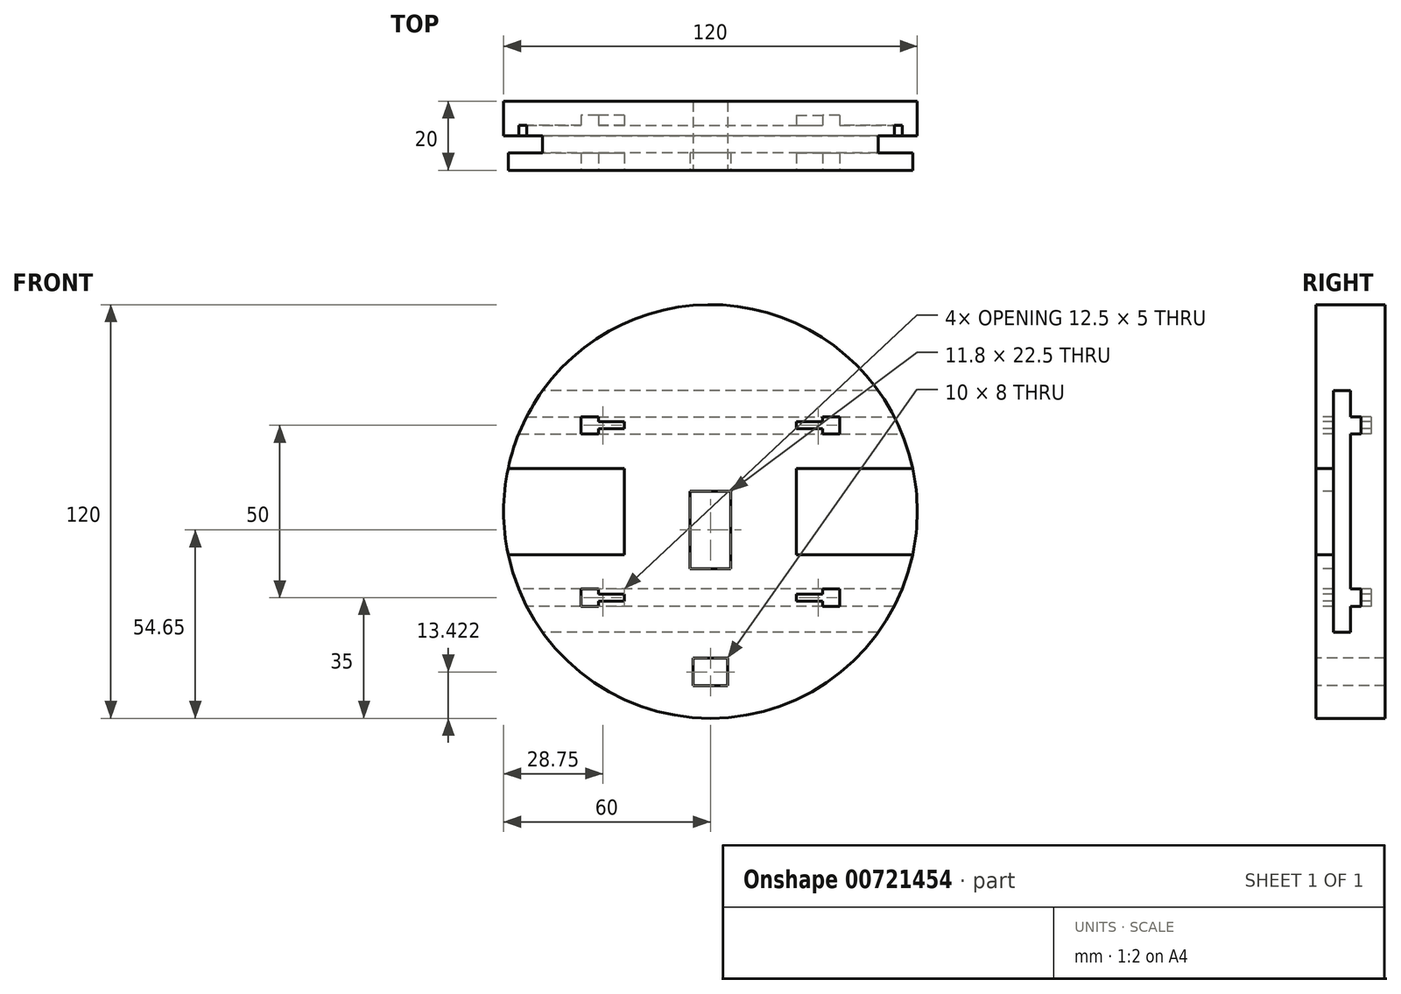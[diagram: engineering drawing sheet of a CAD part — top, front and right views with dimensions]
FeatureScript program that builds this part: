
annotation { "Feature Type Name" : "Feature", "Feature Type Description" : "" }
export const myFeature = defineFeature(function(context is Context, id is Id, definition is map)
    precondition{}
    {
        {
            var Q0;
            Q0=qCreatedBy(makeId("Front.planeOp"),FACE);
            var sketch = newSketch(context, id + "F0", { "sketchPlane" : qUnion([Q0])});
            skCircle(sketch, "E0", {"center": v(0, 0) * mm, "radius": 60 * mm});
            skSolve(sketch);
        }
        {
            var Q0;
            Q0=makeQuery(id+"F0.imprint","IMPRINT",FACE,{"disambiguationData":[TD([[makeQuery(id+"F0.imprint","IMPRINT",EDGE,{"derivedFrom":sQuery(id+"F0.wireOp",EDGE,"E0")}),1.0]])]});
            extrude(context, id + "F1", {"entities" : qUnion([Q0]), "depth" : 20 * mm, "offsetDistance" : 25.4 * mm});
        }
        {
            var Q0;
            Q0=makeQuery(id+"F1.opExtrude","CAP_FACE",FACE,{"disambiguationData":[OSD([sQuery(id+"F0.wireOp",EDGE,"E0")])],"isStart":false});
            var sketch = newSketch(context, id + "F2", { "sketchPlane" : qUnion([Q0])});
            skLineSegment(sketch, "E1.bottom", {"start": v(-60, 12.5) * mm, "end": v(60, 12.5) * mm});
            skLineSegment(sketch, "E1.top", {"start": v(-60, -12.5) * mm, "end": v(60, -12.5) * mm});
            skLineSegment(sketch, "E1.left", {"start": v(-60, 12.5) * mm, "end": v(-60, -12.5) * mm});
            skLineSegment(sketch, "E1.right", {"start": v(60, 12.5) * mm, "end": v(60, -12.5) * mm});
            skPoint(sketch, "E1.middle", {"position": v(0, 0) * mm});
            skLineSegment(sketch, "E2", {"start": v(-25, 12.5) * mm, "end": v(-25, -12.5) * mm});
            skLineSegment(sketch, "E3", {"start": v(25, 12.5) * mm, "end": v(25, -12.5) * mm});
            skSolve(sketch);
        }
        {
            var Q0;
            {var subQ4=sQuery(id+"F2.wireOp",EDGE,"E2");Q0=makeQuery(id+"F2.imprint","IMPRINT",FACE,{"disambiguationData":[TD([[makeQuery(id+"F2.imprint","IMPRINT",EDGE,{"derivedFrom":subQ4}),-1.0]])]});}
            var Q1;
            {var subQ4=sQuery(id+"F2.wireOp",EDGE,"E3");Q1=makeQuery(id+"F2.imprint","IMPRINT",FACE,{"disambiguationData":[TD([[makeQuery(id+"F2.imprint","IMPRINT",EDGE,{"derivedFrom":subQ4}),1.0]])]});}
            extrude(context, id + "F3", {"entities" : qUnion([Q0, Q1]), "operationType" : NewBodyOperationType.REMOVE, "oppositeDirection" : true, "depth" : 10 * mm, "offsetDistance" : 25.4 * mm});
        }
        {
            var Q0;
            Q0=qCreatedBy(makeId("Right.planeOp"),FACE);
            var sketch = newSketch(context, id + "F4", { "sketchPlane" : qUnion([Q0])});
            skPoint(sketch, "E4.middle", {"position": v(0, 0) * mm});
            skLineSegment(sketch, "E5.bottom", {"start": v(-10, 35) * mm, "end": v(-15, 35) * mm});
            skLineSegment(sketch, "E5.top", {"start": v(-10, -35) * mm, "end": v(-15, -35) * mm});
            skLineSegment(sketch, "E5.left", {"start": v(-10, 35) * mm, "end": v(-10, -35) * mm});
            skLineSegment(sketch, "E5.right", {"start": v(-15, 35) * mm, "end": v(-15, -35) * mm});
            skSolve(sketch);
        }
        {
            var Q0;
            Q0 = qSketchRegion(id + "F4", true);
            extrude(context, id + "F5", {"entities" : qUnion([Q0]), "operationType" : NewBodyOperationType.REMOVE, "endBound" : BoundingType.SYMMETRIC, "depth" : 120 * mm, "offsetDistance" : 25.4 * mm});
        }
        {
            var Q0;
            {var subQ0=sQuery(id+"F2.wireOp",EDGE,"E1.top");var subQ1=sQuery(id+"F2.wireOp",EDGE,"E1.bottom");var subQ2=sQuery(id+"F0.wireOp",EDGE,"E0");Q0=makeQuery(id+"F5.boolean.opBoolean","MERGE",FACE,{"derivedFrom":[makeQuery(id+"F3.boolean.opBoolean","COPY",FACE,{"derivedFrom":makeQuery(id+"F3.opExtrude","CAP_FACE",FACE,{"disambiguationData":[OSD([subQ2,subQ1,subQ0,sQuery(id+"F2.wireOp",EDGE,"E2")])],"isStart":false})}),makeQuery(id+"F3.boolean.opBoolean","COPY",FACE,{"derivedFrom":makeQuery(id+"F3.opExtrude","CAP_FACE",FACE,{"disambiguationData":[OSD([subQ2,subQ1,subQ0,sQuery(id+"F2.wireOp",EDGE,"E3")])],"isStart":false})}),makeQuery(id+"F5.opExtrude","SWEPT_FACE",FACE,{"disambiguationData":[OSD([sQuery(id+"F4.wireOp",EDGE,"E5.left")])]})]});}
            var sketch = newSketch(context, id + "F6", { "sketchPlane" : qUnion([Q0])});
            skLineSegment(sketch, "E6.bottom", {"start": v(30, -25) * mm, "end": v(-30, -25) * mm});
            skLineSegment(sketch, "E6.top", {"start": v(30, 25) * mm, "end": v(-30, 25) * mm});
            skLineSegment(sketch, "E6.left", {"start": v(30, -25) * mm, "end": v(30, 25) * mm});
            skLineSegment(sketch, "E6.right", {"start": v(-30, -25) * mm, "end": v(-30, 25) * mm});
            skPoint(sketch, "E6.middle", {"position": v(0, 0) * mm});
            skLineSegment(sketch, "E7.bottom", {"start": v(0, 27.5) * mm, "end": v(-60, 27.5) * mm});
            skLineSegment(sketch, "E7.top", {"start": v(0, 22.5) * mm, "end": v(-60, 22.5) * mm});
            skLineSegment(sketch, "E7.right", {"start": v(-60, 27.5) * mm, "end": v(-60, 22.5) * mm});
            skPoint(sketch, "E7.middle", {"position": v(-30, 25) * mm});
            skLineSegment(sketch, "E8.bottom", {"start": v(0, -22.5) * mm, "end": v(-60, -22.5) * mm});
            skLineSegment(sketch, "E8.top", {"start": v(0, -27.5) * mm, "end": v(-60, -27.5) * mm});
            skLineSegment(sketch, "E8.right", {"start": v(-60, -22.5) * mm, "end": v(-60, -27.5) * mm});
            skPoint(sketch, "E8.middle", {"position": v(-30, -25) * mm});
            skLineSegment(sketch, "E9.bottom", {"start": v(0, 22.5) * mm, "end": v(60, 22.5) * mm});
            skLineSegment(sketch, "E9.top", {"start": v(0, 27.5) * mm, "end": v(60, 27.5) * mm});
            skLineSegment(sketch, "E9.right", {"start": v(60, 22.5) * mm, "end": v(60, 27.5) * mm});
            skPoint(sketch, "E9.middle", {"position": v(30, 25) * mm});
            skLineSegment(sketch, "E10.bottom", {"start": v(0, -22.5) * mm, "end": v(60, -22.5) * mm});
            skLineSegment(sketch, "E10.top", {"start": v(0, -27.5) * mm, "end": v(60, -27.5) * mm});
            skLineSegment(sketch, "E10.right", {"start": v(60, -22.5) * mm, "end": v(60, -27.5) * mm});
            skPoint(sketch, "E10.middle", {"position": v(30, -25) * mm});
            skSolve(sketch);
        }
        {
            var Q0;
            {var subQ1=sQuery(id+"F6.wireOp",EDGE,"E6.bottom");Q0=makeQuery(id+"F6.imprint","IMPRINT",FACE,{"disambiguationData":[TD([[makeQuery(id+"F6.imprint","IMPRINT",EDGE,{"derivedFrom":subQ1}),1.0]])]});}
            var Q1;
            {var subQ8=sQuery(id+"F6.wireOp",EDGE,"E6.top");Q1=makeQuery(id+"F6.imprint","IMPRINT",FACE,{"disambiguationData":[TD([[makeQuery(id+"F6.imprint","IMPRINT",EDGE,{"derivedFrom":subQ8}),-1.0]])]});}
            var Q2;
            {var subQ5=sQuery(id+"F6.wireOp",EDGE,"E6.top");Q2=makeQuery(id+"F6.imprint","IMPRINT",FACE,{"disambiguationData":[TD([[makeQuery(id+"F6.imprint","IMPRINT",EDGE,{"derivedFrom":subQ5}),1.0]])]});}
            var Q3;
            {var subQ6=sQuery(id+"F6.wireOp",EDGE,"E6.bottom");Q3=makeQuery(id+"F6.imprint","IMPRINT",FACE,{"disambiguationData":[TD([[makeQuery(id+"F6.imprint","IMPRINT",EDGE,{"derivedFrom":subQ6}),-1.0]])]});}
            extrude(context, id + "F7", {"entities" : qUnion([Q0, Q1, Q2, Q3]), "operationType" : NewBodyOperationType.REMOVE, "oppositeDirection" : true, "depth" : 3 * mm, "offsetDistance" : 25.4 * mm});
        }
        {
            var Q0;
            Q0=makeQuery(id+"F1.opExtrude","CAP_FACE",FACE,{"disambiguationData":[OSD([sQuery(id+"F0.wireOp",EDGE,"E0")])],"isStart":false});
            var sketch = newSketch(context, id + "F8", { "sketchPlane" : qUnion([Q0])});
            skPoint(sketch, "E11.middle", {"position": v(0, 0) * mm});
            skPoint(sketch, "E12.oppositeSnap0", {"position": v(5.9, 0) * mm});
            skLineSegment(sketch, "E12.bottom", {"start": v(-5.9, 5.9) * mm, "end": v(5.9, 5.9) * mm});
            skLineSegment(sketch, "E12.top", {"start": v(-5.9, -16.6) * mm, "end": v(5.9, -16.6) * mm});
            skLineSegment(sketch, "E12.left", {"start": v(-5.9, 5.9) * mm, "end": v(-5.9, -16.6) * mm});
            skLineSegment(sketch, "E12.right", {"start": v(5.9, 5.9) * mm, "end": v(5.9, -16.6) * mm});
            skSolve(sketch);
        }
        {
            var Q0;
            Q0=makeQuery(id+"F8.imprint","IMPRINT",FACE,{"disambiguationData":[TD([[makeQuery(id+"F8.imprint","IMPRINT",EDGE,{"derivedFrom":sQuery(id+"F8.wireOp",EDGE,"E12.bottom")}),-1.0]])]});
            extrude(context, id + "F9", {"entities" : qUnion([Q0]), "operationType" : NewBodyOperationType.REMOVE, "oppositeDirection" : true, "depth" : 6 * mm, "offsetDistance" : 25.4 * mm});
        }
        {
            var Q0;
            Q0=makeQuery(id+"F1.opExtrude","CAP_FACE",FACE,{"disambiguationData":[OSD([sQuery(id+"F0.wireOp",EDGE,"E0")])],"isStart":false});
            var sketch = newSketch(context, id + "F10", { "sketchPlane" : qUnion([Q0])});
            skLineSegment(sketch, "E13.bottom", {"start": v(35, 25) * mm, "end": v(-35, 25) * mm});
            skLineSegment(sketch, "E13.top", {"start": v(35, -25) * mm, "end": v(-35, -25) * mm});
            skLineSegment(sketch, "E13.left", {"start": v(35, 25) * mm, "end": v(35, -25) * mm});
            skLineSegment(sketch, "E13.right", {"start": v(-35, 25) * mm, "end": v(-35, -25) * mm});
            skPoint(sketch, "E13.middle", {"position": v(0, 0) * mm});
            skLineSegment(sketch, "E14.bottom", {"start": v(-32.5, 27.5) * mm, "end": v(-37.5, 27.5) * mm});
            skLineSegment(sketch, "E14.top", {"start": v(-32.5, 22.5) * mm, "end": v(-37.5, 22.5) * mm});
            skLineSegment(sketch, "E14.left", {"start": v(-32.5, 27.5) * mm, "end": v(-32.5, 22.5) * mm});
            skLineSegment(sketch, "E14.right", {"start": v(-37.5, 27.5) * mm, "end": v(-37.5, 22.5) * mm});
            skPoint(sketch, "E14.middle", {"position": v(-35, 25) * mm});
            skLineSegment(sketch, "E15.bottom", {"start": v(37.5, 27.5) * mm, "end": v(32.5, 27.5) * mm});
            skLineSegment(sketch, "E15.top", {"start": v(37.5, 22.5) * mm, "end": v(32.5, 22.5) * mm});
            skLineSegment(sketch, "E15.left", {"start": v(37.5, 27.5) * mm, "end": v(37.5, 22.5) * mm});
            skLineSegment(sketch, "E15.right", {"start": v(32.5, 27.5) * mm, "end": v(32.5, 22.5) * mm});
            skPoint(sketch, "E15.middle", {"position": v(35, 25) * mm});
            skLineSegment(sketch, "E16.bottom", {"start": v(37.5, -22.5) * mm, "end": v(32.5, -22.5) * mm});
            skLineSegment(sketch, "E16.top", {"start": v(37.5, -27.5) * mm, "end": v(32.5, -27.5) * mm});
            skLineSegment(sketch, "E16.left", {"start": v(37.5, -22.5) * mm, "end": v(37.5, -27.5) * mm});
            skLineSegment(sketch, "E16.right", {"start": v(32.5, -22.5) * mm, "end": v(32.5, -27.5) * mm});
            skPoint(sketch, "E16.middle", {"position": v(35, -25) * mm});
            skLineSegment(sketch, "E17.bottom", {"start": v(-32.5, -22.5) * mm, "end": v(-37.5, -22.5) * mm});
            skLineSegment(sketch, "E17.top", {"start": v(-32.5, -27.5) * mm, "end": v(-37.5, -27.5) * mm});
            skLineSegment(sketch, "E17.left", {"start": v(-32.5, -22.5) * mm, "end": v(-32.5, -27.5) * mm});
            skLineSegment(sketch, "E17.right", {"start": v(-37.5, -22.5) * mm, "end": v(-37.5, -27.5) * mm});
            skPoint(sketch, "E17.middle", {"position": v(-35, -25) * mm});
            skLineSegment(sketch, "E18.bottom", {"start": v(-25, 26) * mm, "end": v(-45, 26) * mm});
            skLineSegment(sketch, "E18.top", {"start": v(-25, 24) * mm, "end": v(-45, 24) * mm});
            skLineSegment(sketch, "E18.left", {"start": v(-25, 26) * mm, "end": v(-25, 24) * mm});
            skLineSegment(sketch, "E18.right", {"start": v(-45, 26) * mm, "end": v(-45, 24) * mm});
            skLineSegment(sketch, "E19.bottom", {"start": v(25, 26) * mm, "end": v(45, 26) * mm});
            skLineSegment(sketch, "E19.top", {"start": v(25, 24) * mm, "end": v(45, 24) * mm});
            skLineSegment(sketch, "E19.left", {"start": v(25, 26) * mm, "end": v(25, 24) * mm});
            skLineSegment(sketch, "E19.right", {"start": v(45, 26) * mm, "end": v(45, 24) * mm});
            skLineSegment(sketch, "E20.bottom", {"start": v(-25, -24) * mm, "end": v(-45, -24) * mm});
            skLineSegment(sketch, "E20.top", {"start": v(-25, -26) * mm, "end": v(-45, -26) * mm});
            skLineSegment(sketch, "E20.left", {"start": v(-25, -24) * mm, "end": v(-25, -26) * mm});
            skLineSegment(sketch, "E20.right", {"start": v(-45, -24) * mm, "end": v(-45, -26) * mm});
            skLineSegment(sketch, "E21.bottom", {"start": v(25, -24) * mm, "end": v(45, -24) * mm});
            skLineSegment(sketch, "E21.top", {"start": v(25, -26) * mm, "end": v(45, -26) * mm});
            skLineSegment(sketch, "E21.left", {"start": v(25, -24) * mm, "end": v(25, -26) * mm});
            skLineSegment(sketch, "E21.right", {"start": v(45, -24) * mm, "end": v(45, -26) * mm});
            skSolve(sketch);
        }
        {
            var Q0;
            {var subQ4=sQuery(id+"F10.wireOp",EDGE,"E14.bottom");Q0=makeQuery(id+"F10.imprint","IMPRINT",FACE,{"disambiguationData":[TD([[makeQuery(id+"F10.imprint","IMPRINT",EDGE,{"derivedFrom":subQ4}),1.0]])]});}
            var Q1;
            {var subQ0=sQuery(id+"F10.wireOp",EDGE,"E13.right");var subQ1=sQuery(id+"F10.wireOp",EDGE,"E13.bottom");var subQ2=makeQuery(id+"F10.imprint","INTERSECT",VERTEX,{"derivedFrom":[subQ1,subQ0]});Q1=makeQuery(id+"F10.imprint","IMPRINT",FACE,{"disambiguationData":[TD([[makeQuery(id+"F10.imprint","IMPRINT",EDGE,{"disambiguationData":[TD([[subQ2,1.0]])],"derivedFrom":subQ1}),1.0]])]});}
            var Q2;
            {var subQ4=sQuery(id+"F10.wireOp",EDGE,"E15.bottom");Q2=makeQuery(id+"F10.imprint","IMPRINT",FACE,{"disambiguationData":[TD([[makeQuery(id+"F10.imprint","IMPRINT",EDGE,{"derivedFrom":subQ4}),1.0]])]});}
            var Q3;
            {var subQ0=sQuery(id+"F10.wireOp",EDGE,"E13.left");var subQ1=sQuery(id+"F10.wireOp",EDGE,"E13.bottom");var subQ2=makeQuery(id+"F10.imprint","INTERSECT",VERTEX,{"derivedFrom":[subQ1,subQ0]});Q3=makeQuery(id+"F10.imprint","IMPRINT",FACE,{"disambiguationData":[TD([[makeQuery(id+"F10.imprint","IMPRINT",EDGE,{"disambiguationData":[TD([[subQ2,-1.0]])],"derivedFrom":subQ1}),1.0]])]});}
            var Q4;
            {var subQ0=sQuery(id+"F10.wireOp",EDGE,"E16.top");Q4=makeQuery(id+"F10.imprint","IMPRINT",FACE,{"disambiguationData":[TD([[makeQuery(id+"F10.imprint","IMPRINT",EDGE,{"derivedFrom":subQ0}),-1.0]])]});}
            var Q5;
            {var subQ0=sQuery(id+"F10.wireOp",EDGE,"E13.left");var subQ1=sQuery(id+"F10.wireOp",EDGE,"E13.top");var subQ2=makeQuery(id+"F10.imprint","INTERSECT",VERTEX,{"derivedFrom":[subQ1,subQ0]});Q5=makeQuery(id+"F10.imprint","IMPRINT",FACE,{"disambiguationData":[TD([[makeQuery(id+"F10.imprint","IMPRINT",EDGE,{"disambiguationData":[TD([[subQ2,-1.0]])],"derivedFrom":subQ1}),-1.0]])]});}
            var Q6;
            {var subQ0=sQuery(id+"F10.wireOp",EDGE,"E17.top");Q6=makeQuery(id+"F10.imprint","IMPRINT",FACE,{"disambiguationData":[TD([[makeQuery(id+"F10.imprint","IMPRINT",EDGE,{"derivedFrom":subQ0}),-1.0]])]});}
            var Q7;
            {var subQ0=sQuery(id+"F10.wireOp",EDGE,"E13.right");var subQ1=sQuery(id+"F10.wireOp",EDGE,"E13.top");var subQ2=makeQuery(id+"F10.imprint","INTERSECT",VERTEX,{"derivedFrom":[subQ1,subQ0]});Q7=makeQuery(id+"F10.imprint","IMPRINT",FACE,{"disambiguationData":[TD([[makeQuery(id+"F10.imprint","IMPRINT",EDGE,{"disambiguationData":[TD([[subQ2,1.0]])],"derivedFrom":subQ1}),-1.0]])]});}
            var Q8;
            {var subQ1=sQuery(id+"F10.wireOp",EDGE,"E13.bottom");var subQ9=sQuery(id+"F10.wireOp",EDGE,"E13.left");var subQ10=makeQuery(id+"F10.imprint","INTERSECT",VERTEX,{"derivedFrom":[subQ1,subQ9]});Q8=makeQuery(id+"F10.imprint","IMPRINT",FACE,{"disambiguationData":[TD([[makeQuery(id+"F10.imprint","IMPRINT",EDGE,{"disambiguationData":[TD([[subQ10,-1.0]])],"derivedFrom":subQ1}),-1.0]])]});}
            var Q9;
            {var subQ0=sQuery(id+"F10.wireOp",EDGE,"E19.top");var subQ1=sQuery(id+"F10.wireOp",EDGE,"E13.left");var subQ2=makeQuery(id+"F10.imprint","INTERSECT",VERTEX,{"derivedFrom":[subQ1,subQ0]});Q9=makeQuery(id+"F10.imprint","IMPRINT",FACE,{"disambiguationData":[TD([[makeQuery(id+"F10.imprint","IMPRINT",EDGE,{"disambiguationData":[TD([[subQ2,-1.0]])],"derivedFrom":subQ1}),1.0]])]});}
            var Q10;
            {var subQ0=sQuery(id+"F10.wireOp",EDGE,"E19.top");var subQ1=sQuery(id+"F10.wireOp",EDGE,"E13.left");var subQ2=makeQuery(id+"F10.imprint","INTERSECT",VERTEX,{"derivedFrom":[subQ1,subQ0]});Q10=makeQuery(id+"F10.imprint","IMPRINT",FACE,{"disambiguationData":[TD([[makeQuery(id+"F10.imprint","IMPRINT",EDGE,{"disambiguationData":[TD([[subQ2,-1.0]])],"derivedFrom":subQ1}),-1.0]])]});}
            var Q11;
            {var subQ0=sQuery(id+"F10.wireOp",EDGE,"E15.right");var subQ1=sQuery(id+"F10.wireOp",EDGE,"E13.bottom");var subQ2=makeQuery(id+"F10.imprint","INTERSECT",VERTEX,{"derivedFrom":[subQ1,subQ0]});Q11=makeQuery(id+"F10.imprint","IMPRINT",FACE,{"disambiguationData":[TD([[makeQuery(id+"F10.imprint","IMPRINT",EDGE,{"disambiguationData":[TD([[subQ2,-1.0]])],"derivedFrom":subQ1}),1.0]])]});}
            var Q12;
            {var subQ0=sQuery(id+"F10.wireOp",EDGE,"E15.right");var subQ1=sQuery(id+"F10.wireOp",EDGE,"E13.bottom");var subQ2=makeQuery(id+"F10.imprint","INTERSECT",VERTEX,{"derivedFrom":[subQ1,subQ0]});Q12=makeQuery(id+"F10.imprint","IMPRINT",FACE,{"disambiguationData":[TD([[makeQuery(id+"F10.imprint","IMPRINT",EDGE,{"disambiguationData":[TD([[subQ2,-1.0]])],"derivedFrom":subQ1}),-1.0]])]});}
            var Q13;
            {var subQ5=sQuery(id+"F10.wireOp",EDGE,"E13.right");var subQ6=sQuery(id+"F10.wireOp",EDGE,"E13.top");var subQ7=makeQuery(id+"F10.imprint","INTERSECT",VERTEX,{"derivedFrom":[subQ6,subQ5]});Q13=makeQuery(id+"F10.imprint","IMPRINT",FACE,{"disambiguationData":[TD([[makeQuery(id+"F10.imprint","IMPRINT",EDGE,{"disambiguationData":[TD([[subQ7,1.0]])],"derivedFrom":subQ6}),1.0]])]});}
            var Q14;
            {var subQ0=sQuery(id+"F10.wireOp",EDGE,"E17.bottom");var subQ1=sQuery(id+"F10.wireOp",EDGE,"E13.right");var subQ2=makeQuery(id+"F10.imprint","INTERSECT",VERTEX,{"derivedFrom":[subQ1,subQ0]});Q14=makeQuery(id+"F10.imprint","IMPRINT",FACE,{"disambiguationData":[TD([[makeQuery(id+"F10.imprint","IMPRINT",EDGE,{"disambiguationData":[TD([[subQ2,-1.0]])],"derivedFrom":subQ1}),1.0]])]});}
            var Q15;
            {var subQ0=sQuery(id+"F10.wireOp",EDGE,"E17.bottom");var subQ1=sQuery(id+"F10.wireOp",EDGE,"E13.right");var subQ2=makeQuery(id+"F10.imprint","INTERSECT",VERTEX,{"derivedFrom":[subQ1,subQ0]});Q15=makeQuery(id+"F10.imprint","IMPRINT",FACE,{"disambiguationData":[TD([[makeQuery(id+"F10.imprint","IMPRINT",EDGE,{"disambiguationData":[TD([[subQ2,-1.0]])],"derivedFrom":subQ1}),-1.0]])]});}
            var Q16;
            {var subQ0=sQuery(id+"F10.wireOp",EDGE,"E20.left");var subQ1=sQuery(id+"F10.wireOp",EDGE,"E13.top");var subQ2=makeQuery(id+"F10.imprint","INTERSECT",VERTEX,{"derivedFrom":[subQ1,subQ0]});Q16=makeQuery(id+"F10.imprint","IMPRINT",FACE,{"disambiguationData":[TD([[makeQuery(id+"F10.imprint","IMPRINT",EDGE,{"disambiguationData":[TD([[subQ2,-1.0]])],"derivedFrom":subQ1}),-1.0]])]});}
            var Q17;
            {var subQ0=sQuery(id+"F10.wireOp",EDGE,"E20.left");var subQ1=sQuery(id+"F10.wireOp",EDGE,"E13.top");var subQ2=makeQuery(id+"F10.imprint","INTERSECT",VERTEX,{"derivedFrom":[subQ1,subQ0]});Q17=makeQuery(id+"F10.imprint","IMPRINT",FACE,{"disambiguationData":[TD([[makeQuery(id+"F10.imprint","IMPRINT",EDGE,{"disambiguationData":[TD([[subQ2,-1.0]])],"derivedFrom":subQ1}),1.0]])]});}
            var Q18;
            {var subQ1=sQuery(id+"F10.wireOp",EDGE,"E13.top");var subQ6=sQuery(id+"F10.wireOp",EDGE,"E13.left");var subQ11=makeQuery(id+"F10.imprint","INTERSECT",VERTEX,{"derivedFrom":[subQ1,subQ6]});Q18=makeQuery(id+"F10.imprint","IMPRINT",FACE,{"disambiguationData":[TD([[makeQuery(id+"F10.imprint","IMPRINT",EDGE,{"disambiguationData":[TD([[subQ11,-1.0]])],"derivedFrom":subQ1}),1.0]])]});}
            var Q19;
            {var subQ0=sQuery(id+"F10.wireOp",EDGE,"E16.bottom");var subQ1=sQuery(id+"F10.wireOp",EDGE,"E13.left");var subQ2=makeQuery(id+"F10.imprint","INTERSECT",VERTEX,{"derivedFrom":[subQ1,subQ0]});Q19=makeQuery(id+"F10.imprint","IMPRINT",FACE,{"disambiguationData":[TD([[makeQuery(id+"F10.imprint","IMPRINT",EDGE,{"disambiguationData":[TD([[subQ2,-1.0]])],"derivedFrom":subQ1}),1.0]])]});}
            var Q20;
            {var subQ0=sQuery(id+"F10.wireOp",EDGE,"E16.bottom");var subQ1=sQuery(id+"F10.wireOp",EDGE,"E13.left");var subQ2=makeQuery(id+"F10.imprint","INTERSECT",VERTEX,{"derivedFrom":[subQ1,subQ0]});Q20=makeQuery(id+"F10.imprint","IMPRINT",FACE,{"disambiguationData":[TD([[makeQuery(id+"F10.imprint","IMPRINT",EDGE,{"disambiguationData":[TD([[subQ2,-1.0]])],"derivedFrom":subQ1}),-1.0]])]});}
            var Q21;
            {var subQ1=sQuery(id+"F10.wireOp",EDGE,"E13.bottom");var subQ5=sQuery(id+"F10.wireOp",EDGE,"E13.right");var subQ6=makeQuery(id+"F10.imprint","INTERSECT",VERTEX,{"derivedFrom":[subQ1,subQ5]});Q21=makeQuery(id+"F10.imprint","IMPRINT",FACE,{"disambiguationData":[TD([[makeQuery(id+"F10.imprint","IMPRINT",EDGE,{"disambiguationData":[TD([[subQ6,1.0]])],"derivedFrom":subQ1}),-1.0]])]});}
            var Q22;
            {var subQ0=sQuery(id+"F10.wireOp",EDGE,"E18.top");var subQ1=sQuery(id+"F10.wireOp",EDGE,"E13.right");var subQ2=makeQuery(id+"F10.imprint","INTERSECT",VERTEX,{"derivedFrom":[subQ1,subQ0]});Q22=makeQuery(id+"F10.imprint","IMPRINT",FACE,{"disambiguationData":[TD([[makeQuery(id+"F10.imprint","IMPRINT",EDGE,{"disambiguationData":[TD([[subQ2,-1.0]])],"derivedFrom":subQ1}),-1.0]])]});}
            var Q23;
            {var subQ0=sQuery(id+"F10.wireOp",EDGE,"E18.top");var subQ1=sQuery(id+"F10.wireOp",EDGE,"E13.right");var subQ2=makeQuery(id+"F10.imprint","INTERSECT",VERTEX,{"derivedFrom":[subQ1,subQ0]});Q23=makeQuery(id+"F10.imprint","IMPRINT",FACE,{"disambiguationData":[TD([[makeQuery(id+"F10.imprint","IMPRINT",EDGE,{"disambiguationData":[TD([[subQ2,-1.0]])],"derivedFrom":subQ1}),1.0]])]});}
            var Q24;
            {var subQ0=sQuery(id+"F10.wireOp",EDGE,"E18.left");var subQ1=sQuery(id+"F10.wireOp",EDGE,"E13.bottom");var subQ2=makeQuery(id+"F10.imprint","INTERSECT",VERTEX,{"derivedFrom":[subQ1,subQ0]});Q24=makeQuery(id+"F10.imprint","IMPRINT",FACE,{"disambiguationData":[TD([[makeQuery(id+"F10.imprint","IMPRINT",EDGE,{"disambiguationData":[TD([[subQ2,-1.0]])],"derivedFrom":subQ1}),-1.0]])]});}
            var Q25;
            {var subQ0=sQuery(id+"F10.wireOp",EDGE,"E18.left");var subQ1=sQuery(id+"F10.wireOp",EDGE,"E13.bottom");var subQ2=makeQuery(id+"F10.imprint","INTERSECT",VERTEX,{"derivedFrom":[subQ1,subQ0]});Q25=makeQuery(id+"F10.imprint","IMPRINT",FACE,{"disambiguationData":[TD([[makeQuery(id+"F10.imprint","IMPRINT",EDGE,{"disambiguationData":[TD([[subQ2,-1.0]])],"derivedFrom":subQ1}),1.0]])]});}
            var Q26;
            {var subQ0=sQuery(id+"F10.wireOp",EDGE,"E16.right");var subQ1=sQuery(id+"F10.wireOp",EDGE,"E13.top");var subQ2=makeQuery(id+"F10.imprint","INTERSECT",VERTEX,{"derivedFrom":[subQ1,subQ0]});Q26=makeQuery(id+"F10.imprint","IMPRINT",FACE,{"disambiguationData":[TD([[makeQuery(id+"F10.imprint","IMPRINT",EDGE,{"disambiguationData":[TD([[subQ2,-1.0]])],"derivedFrom":subQ1}),1.0]])]});}
            var Q27;
            {var subQ0=sQuery(id+"F10.wireOp",EDGE,"E16.right");var subQ1=sQuery(id+"F10.wireOp",EDGE,"E13.top");var subQ2=makeQuery(id+"F10.imprint","INTERSECT",VERTEX,{"derivedFrom":[subQ1,subQ0]});Q27=makeQuery(id+"F10.imprint","IMPRINT",FACE,{"disambiguationData":[TD([[makeQuery(id+"F10.imprint","IMPRINT",EDGE,{"disambiguationData":[TD([[subQ2,-1.0]])],"derivedFrom":subQ1}),-1.0]])]});}
            extrude(context, id + "F11", {"entities" : qUnion([Q0, Q1, Q2, Q3, Q4, Q5, Q6, Q7, Q8, Q9, Q10, Q11, Q12, Q13, Q14, Q15, Q16, Q17, Q18, Q19, Q20, Q21, Q22, Q23, Q24, Q25, Q26, Q27]), "operationType" : NewBodyOperationType.REMOVE, "oppositeDirection" : true, "depth" : 16 * mm, "offsetDistance" : 25.4 * mm});
        }
        {
            var Q0;
            Q0=makeQuery(id+"F1.opExtrude","CAP_FACE",FACE,{"disambiguationData":[OSD([sQuery(id+"F0.wireOp",EDGE,"E0")])],"isStart":false});
            var sketch = newSketch(context, id + "F12", { "sketchPlane" : qUnion([Q0])});
            skLineSegment(sketch, "E22.bottom", {"start": v(-5, -42.58) * mm, "end": v(5, -42.58) * mm});
            skLineSegment(sketch, "E22.top", {"start": v(-5, -50.58) * mm, "end": v(5, -50.58) * mm});
            skLineSegment(sketch, "E22.left", {"start": v(-5, -42.58) * mm, "end": v(-5, -50.58) * mm});
            skLineSegment(sketch, "E22.right", {"start": v(5, -42.58) * mm, "end": v(5, -50.58) * mm});
            skSolve(sketch);
        }
        {
            var Q0;
            Q0=makeQuery(id+"F12.imprint","IMPRINT",FACE,{"disambiguationData":[TD([[makeQuery(id+"F12.imprint","IMPRINT",EDGE,{"derivedFrom":sQuery(id+"F12.wireOp",EDGE,"E22.bottom")}),-1.0]])]});
            extrude(context, id + "F13", {"entities" : qUnion([Q0]), "operationType" : NewBodyOperationType.REMOVE, "endBound" : BoundingType.THROUGH_ALL, "oppositeDirection" : true, "depth" : 25.4 * mm, "offsetDistance" : 25.4 * mm});
        }
    });
